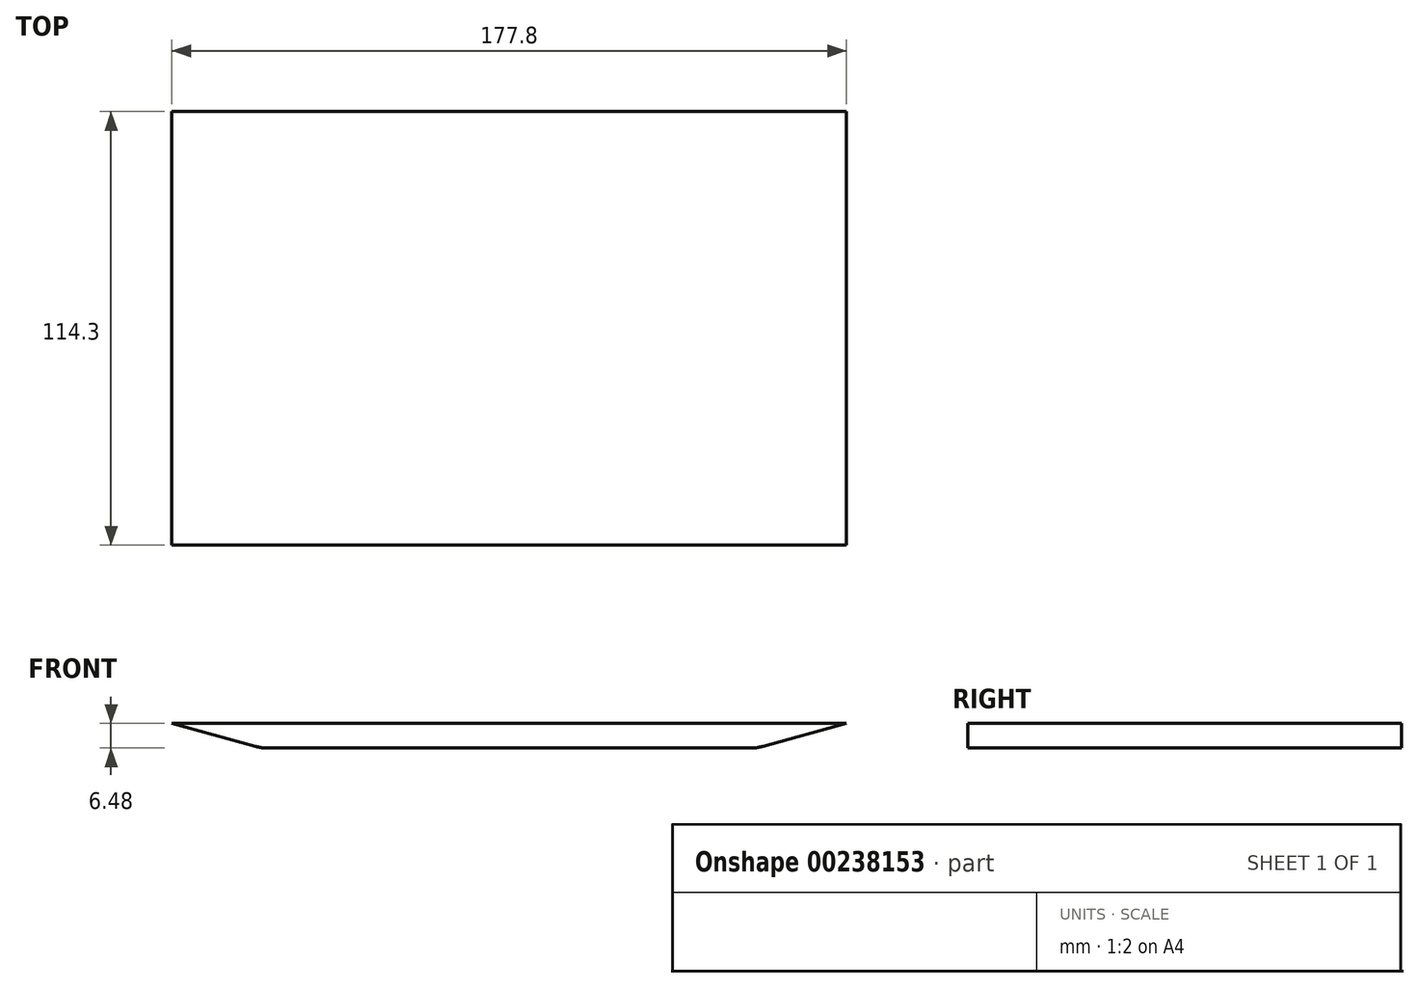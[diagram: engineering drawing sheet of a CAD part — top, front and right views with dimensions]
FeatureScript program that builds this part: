
annotation { "Feature Type Name" : "Feature", "Feature Type Description" : "" }
export const myFeature = defineFeature(function(context is Context, id is Id, definition is map)
    precondition{}
    {
        {
            var Q0;
            Q0=qCreatedBy(makeId("Front.planeOp"),FACE);
            var sketch = newSketch(context, id + "F0", { "sketchPlane" : qUnion([Q0])});
            skLineSegment(sketch, "E0", {"start": v(-90.44, 0) * mm, "end": v(87.36, 0) * mm});
            skLineSegment(sketch, "E1", {"start": v(87.36, 0) * mm, "end": v(65.3, -6.03) * mm});
            skLineSegment(sketch, "E2", {"start": v(61.96, -6.48) * mm, "end": v(-65.04, -6.48) * mm});
            skLineSegment(sketch, "E3", {"start": v(-68.4, -6.03) * mm, "end": v(-90.44, 0) * mm});
            skArc(sketch, "E4.filletArc", {"start": v(61.96, -6.48) * mm, "mid": v(63.65, -6.37) * mm, "end": v(65.3, -6.03) * mm});
            skArc(sketch, "E5.filletArc", {"start": v(-68.4, -6.03) * mm, "mid": v(-66.73, -6.37) * mm, "end": v(-65.04, -6.48) * mm});
            skSolve(sketch);
        }
        {
            var Q0;
            Q0=makeQuery(id+"F0.imprint","IMPRINT",FACE,{"disambiguationData":[TD([[makeQuery(id+"F0.imprint","IMPRINT",EDGE,{"derivedFrom":sQuery(id+"F0.wireOp",EDGE,"E0")}),-1.0]])]});
            extrude(context, id + "F1", {"entities" : qUnion([Q0]), "depth" : 57.15 * mm, "hasSecondDirection" : true, "secondDirectionOppositeDirection" : true, "secondDirectionDepth" : 57.15 * mm});
        }
    });
